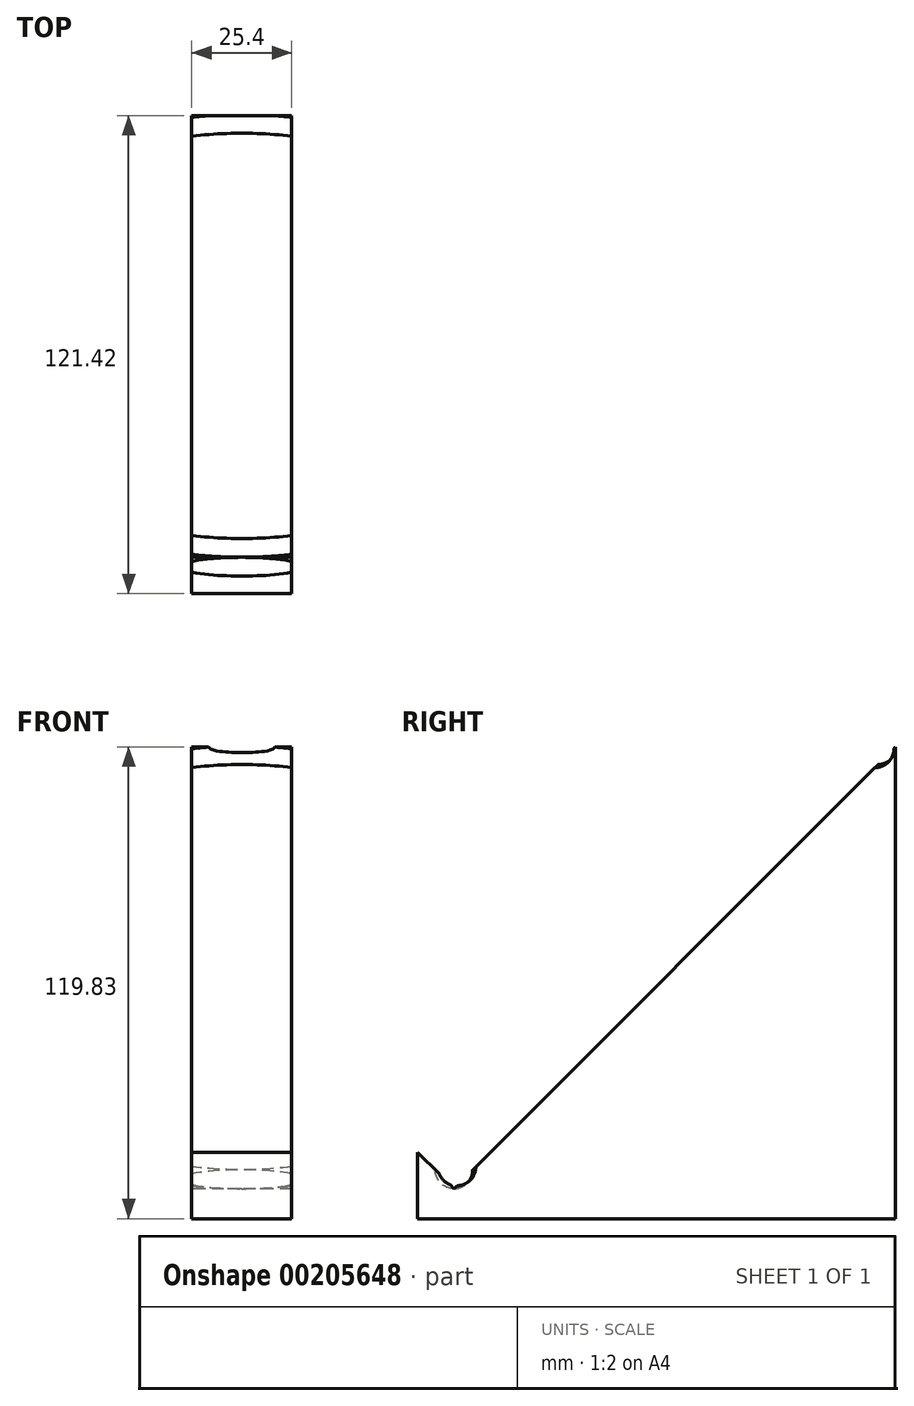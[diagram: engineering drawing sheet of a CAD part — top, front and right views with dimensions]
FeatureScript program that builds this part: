
annotation { "Feature Type Name" : "Feature", "Feature Type Description" : "" }
export const myFeature = defineFeature(function(context is Context, id is Id, definition is map)
    precondition{}
    {
        {
            var Q0;
            Q0=qCreatedBy(makeId("Right.planeOp"),FACE);
            var sketch = newSketch(context, id + "F0", { "sketchPlane" : qUnion([Q0])});
            skLineSegment(sketch, "E0", {"start": v(0, 0) * mm, "end": v(121.42, 0) * mm});
            skLineSegment(sketch, "E1", {"start": v(121.42, 0) * mm, "end": v(121.42, 107.76) * mm});
            skLineSegment(sketch, "E2", {"start": v(121.42, 107.76) * mm, "end": v(13.65, 0) * mm});
            skLineSegment(sketch, "E3", {"start": v(13.65, 0) * mm, "end": v(0, 13.65) * mm});
            skLineSegment(sketch, "E4", {"start": v(0, 13.65) * mm, "end": v(0, 0) * mm});
            skLineSegment(sketch, "E5", {"start": v(121.42, 0) * mm, "end": v(121.42, -3.17) * mm});
            skLineSegment(sketch, "E6", {"start": v(121.42, -3.17) * mm, "end": v(0, -3.18) * mm});
            skLineSegment(sketch, "E7", {"start": v(0, -3.18) * mm, "end": v(0, 0) * mm});
            skLineSegment(sketch, "E8", {"start": v(13.65, 0) * mm, "end": v(9.2, 4.45) * mm});
            skLineSegment(sketch, "E9", {"start": v(9.2, 4.45) * mm, "end": v(116.97, 112.2) * mm});
            skLineSegment(sketch, "E10", {"start": v(116.97, 112.2) * mm, "end": v(121.42, 107.76) * mm});
            skLineSegment(sketch, "E11", {"start": v(116.97, 112.2) * mm, "end": v(121.42, 116.65) * mm});
            skLineSegment(sketch, "E12", {"start": v(121.42, 116.65) * mm, "end": v(121.42, 107.76) * mm});
            skSolve(sketch);
        }
        {
            var Q0;
            Q0=qSketchRegion(id+"F0",true);
            extrude(context, id + "F1", {"entities" : qUnion([Q0]), "depth" : 12.7 * mm, "hasSecondDirection" : true, "secondDirectionOppositeDirection" : true, "secondDirectionDepth" : 12.7 * mm});
        }
        {
            var Q0;
            Q0=qCreatedBy(makeId("Right.planeOp"),FACE);
            var sketch = newSketch(context, id + "F2", { "sketchPlane" : qUnion([Q0])});
            skLineSegment(sketch, "E13", {"start": v(0, 0) * mm, "end": v(9.2, 0) * mm, "construction": true});
            skLineSegment(sketch, "E14", {"start": v(9.2, 0) * mm, "end": v(9.2, 9.2) * mm, "construction": true});
            skLineSegment(sketch, "E15", {"start": v(9.2, 9.2) * mm, "end": v(63.09, 9.2) * mm, "construction": true});
            skLineSegment(sketch, "E16", {"start": v(63.09, 9.2) * mm, "end": v(63.09, 63.09) * mm, "construction": true});
            skLineSegment(sketch, "E17", {"start": v(63.09, 63.09) * mm, "end": v(9.2, 9.2) * mm, "construction": true});
            skCircle(sketch, "E18", {"center": v(9.2, 9.2) * mm, "radius": 4.76 * mm});
            skLineSegment(sketch, "E19", {"start": v(63.09, 63.09) * mm, "end": v(50.94, 75.23) * mm, "construction": true});
            skSolve(sketch);
        }
        {
            var Q0;
            Q0=qSketchRegion(id+"F2",true);
            var Q1;
            Q1=sQuery(id+"F2.wireOp",EDGE,"E19");
            revolve(context, id + "F3", {"operationType" : NewBodyOperationType.REMOVE, "entities" : qUnion([Q0]), "axis" : qUnion([Q1]), "revolveType" : RevolveType.FULL, "oppositeDirection" : true});
        }
    });
